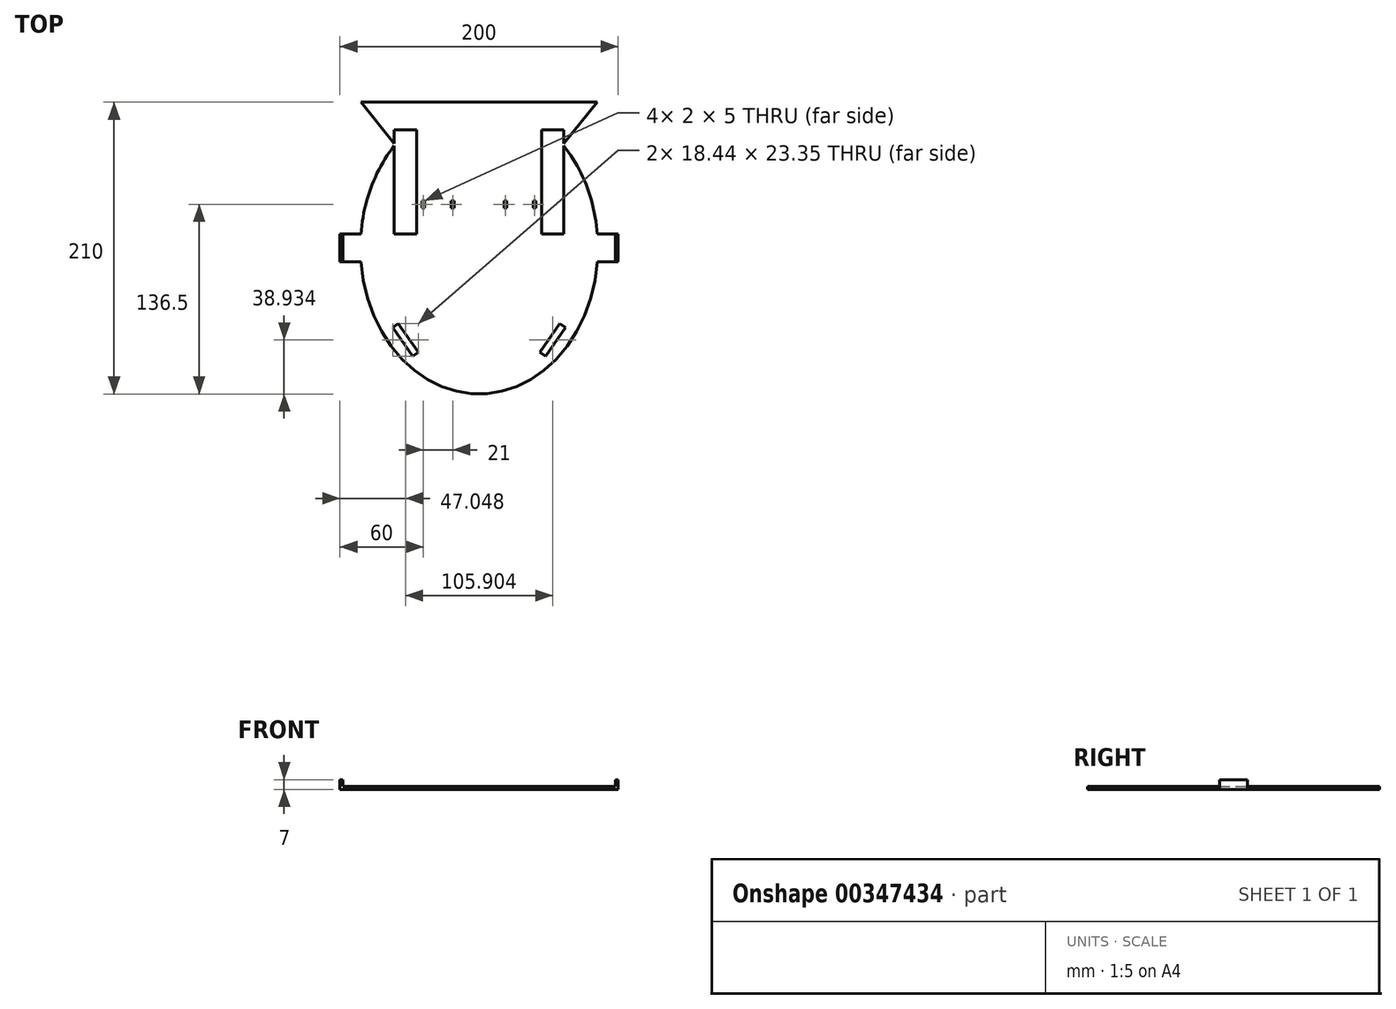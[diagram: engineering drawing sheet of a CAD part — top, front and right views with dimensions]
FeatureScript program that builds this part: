
annotation { "Feature Type Name" : "Feature", "Feature Type Description" : "" }
export const myFeature = defineFeature(function(context is Context, id is Id, definition is map)
    precondition{}
    {
        {
            var Q0;
            Q0=qCreatedBy(makeId("Top.planeOp"),FACE);
            var sketch = newSketch(context, id + "F0", { "sketchPlane" : qUnion([Q0])});
            skLineSegment(sketch, "E0.bottom", {"start": v(0, 0) * mm, "end": v(170, 0) * mm});
            skLineSegment(sketch, "E0.top", {"start": v(0, 210) * mm, "end": v(170, 210) * mm});
            skLineSegment(sketch, "E0.left", {"start": v(0, 0) * mm, "end": v(0, 210) * mm});
            skLineSegment(sketch, "E0.right", {"start": v(170, 0) * mm, "end": v(170, 210) * mm});
            skLineSegment(sketch, "E1", {"start": v(-48.12, 105) * mm, "end": v(198.12, 105) * mm, "construction": true});
            skSolve(sketch);
        }
        {
            var Q0;
            Q0=makeQuery(id+"F0.imprint","IMPRINT",FACE,{"disambiguationData":[TD([[makeQuery(id+"F0.imprint","IMPRINT",EDGE,{"derivedFrom":sQuery(id+"F0.wireOp",EDGE,"E0.bottom")}),1.0]])]});
            extrude(context, id + "F1", {"entities" : qUnion([Q0]), "depth" : 2 * mm});
        }
        {
            var Q0;
            Q0=makeQuery(id+"F1.opExtrude","CAP_FACE",FACE,{"disambiguationData":[OSD([sQuery(id+"F0.wireOp",EDGE,"E0.bottom"),sQuery(id+"F0.wireOp",EDGE,"E0.top"),sQuery(id+"F0.wireOp",EDGE,"E0.left"),sQuery(id+"F0.wireOp",EDGE,"E0.right")])],"isStart":false});
            var sketch = newSketch(context, id + "F2", { "sketchPlane" : qUnion([Q0])});
            skLineSegment(sketch, "E2.bottom", {"start": v(0, 95) * mm, "end": v(-15, 95) * mm});
            skLineSegment(sketch, "E2.top", {"start": v(0, 115) * mm, "end": v(-15, 115) * mm});
            skLineSegment(sketch, "E2.left", {"start": v(0, 95) * mm, "end": v(0, 115) * mm});
            skLineSegment(sketch, "E2.right", {"start": v(-15, 95) * mm, "end": v(-15, 115) * mm});
            skLineSegment(sketch, "E3.bottom", {"start": v(170, 95) * mm, "end": v(185, 95) * mm});
            skLineSegment(sketch, "E3.top", {"start": v(170, 115) * mm, "end": v(185, 115) * mm});
            skLineSegment(sketch, "E3.left", {"start": v(170, 95) * mm, "end": v(170, 115) * mm});
            skLineSegment(sketch, "E3.right", {"start": v(185, 95) * mm, "end": v(185, 115) * mm});
            skSolve(sketch);
        }
        {
            var Q0;
            Q0=makeQuery(id+"F2.imprint","IMPRINT",FACE,{"disambiguationData":[TD([[makeQuery(id+"F2.imprint","IMPRINT",EDGE,{"derivedFrom":sQuery(id+"F2.wireOp",EDGE,"E2.bottom")}),-1.0]])]});
            var Q1;
            Q1=makeQuery(id+"F2.imprint","IMPRINT",FACE,{"disambiguationData":[TD([[makeQuery(id+"F2.imprint","IMPRINT",EDGE,{"derivedFrom":sQuery(id+"F2.wireOp",EDGE,"E3.bottom")}),1.0]])]});
            extrude(context, id + "F3", {"entities" : qUnion([Q0, Q1]), "operationType" : NewBodyOperationType.ADD, "oppositeDirection" : true, "depth" : 2 * mm});
        }
        {
            var Q0;
            Q0=makeQuery(id+"F3.boolean.opBoolean","MERGE",FACE,{"derivedFrom":[makeQuery(id+"F1.opExtrude","CAP_FACE",FACE,{"disambiguationData":[OSD([sQuery(id+"F0.wireOp",EDGE,"E0.bottom"),sQuery(id+"F0.wireOp",EDGE,"E0.top"),sQuery(id+"F0.wireOp",EDGE,"E0.left"),sQuery(id+"F0.wireOp",EDGE,"E0.right")])],"isStart":false}),makeQuery(id+"F3.opExtrude","CAP_FACE",FACE,{"disambiguationData":[OSD([sQuery(id+"F2.wireOp",EDGE,"E2.bottom"),sQuery(id+"F2.wireOp",EDGE,"E2.top"),sQuery(id+"F2.wireOp",EDGE,"E2.left"),sQuery(id+"F2.wireOp",EDGE,"E2.right")])],"isStart":true}),makeQuery(id+"F3.opExtrude","CAP_FACE",FACE,{"disambiguationData":[OSD([sQuery(id+"F2.wireOp",EDGE,"E3.bottom"),sQuery(id+"F2.wireOp",EDGE,"E3.top"),sQuery(id+"F2.wireOp",EDGE,"E3.left"),sQuery(id+"F2.wireOp",EDGE,"E3.right")])],"isStart":true})]});
            var sketch = newSketch(context, id + "F4", { "sketchPlane" : qUnion([Q0])});
            skLineSegment(sketch, "E4.bottom", {"start": v(-15, 95) * mm, "end": v(-13, 95) * mm});
            skLineSegment(sketch, "E4.top", {"start": v(-15, 115) * mm, "end": v(-13, 115) * mm});
            skLineSegment(sketch, "E4.left", {"start": v(-15, 95) * mm, "end": v(-15, 115) * mm});
            skLineSegment(sketch, "E4.right", {"start": v(-13, 95) * mm, "end": v(-13, 115) * mm});
            skLineSegment(sketch, "E5.bottom", {"start": v(185, 95) * mm, "end": v(183, 95) * mm});
            skLineSegment(sketch, "E5.top", {"start": v(185, 115) * mm, "end": v(183, 115) * mm});
            skLineSegment(sketch, "E5.left", {"start": v(185, 95) * mm, "end": v(185, 115) * mm});
            skLineSegment(sketch, "E5.right", {"start": v(183, 95) * mm, "end": v(183, 115) * mm});
            skSolve(sketch);
        }
        {
            var Q0;
            Q0=makeQuery(id+"F4.imprint","IMPRINT",FACE,{"disambiguationData":[TD([[makeQuery(id+"F4.imprint","IMPRINT",EDGE,{"derivedFrom":sQuery(id+"F4.wireOp",EDGE,"E5.bottom")}),1.0]])]});
            var Q1;
            Q1=makeQuery(id+"F4.imprint","IMPRINT",FACE,{"disambiguationData":[TD([[makeQuery(id+"F4.imprint","IMPRINT",EDGE,{"derivedFrom":sQuery(id+"F4.wireOp",EDGE,"E4.bottom")}),-1.0]])]});
            extrude(context, id + "F5", {"entities" : qUnion([Q0, Q1]), "operationType" : NewBodyOperationType.ADD, "depth" : 5 * mm});
        }
        {
            var Q0;
            Q0=makeQuery(id+"F3.boolean.opBoolean","MERGE",FACE,{"derivedFrom":[makeQuery(id+"F1.opExtrude","CAP_FACE",FACE,{"disambiguationData":[OSD([sQuery(id+"F0.wireOp",EDGE,"E0.bottom"),sQuery(id+"F0.wireOp",EDGE,"E0.top"),sQuery(id+"F0.wireOp",EDGE,"E0.left"),sQuery(id+"F0.wireOp",EDGE,"E0.right")])],"isStart":false}),makeQuery(id+"F3.opExtrude","CAP_FACE",FACE,{"disambiguationData":[OSD([sQuery(id+"F2.wireOp",EDGE,"E2.bottom"),sQuery(id+"F2.wireOp",EDGE,"E2.top"),sQuery(id+"F2.wireOp",EDGE,"E2.left"),sQuery(id+"F2.wireOp",EDGE,"E2.right")])],"isStart":true}),makeQuery(id+"F3.opExtrude","CAP_FACE",FACE,{"disambiguationData":[OSD([sQuery(id+"F2.wireOp",EDGE,"E3.bottom"),sQuery(id+"F2.wireOp",EDGE,"E3.top"),sQuery(id+"F2.wireOp",EDGE,"E3.left"),sQuery(id+"F2.wireOp",EDGE,"E3.right")])],"isStart":true})]});
            var sketch = newSketch(context, id + "F6", { "sketchPlane" : qUnion([Q0])});
            skEllipse(sketch, "E6", {"center": v(85, 105) * mm, "majorRadius": 105 * mm, "minorRadius": 85.39 * mm, "majorAxis": v(0, -1)});
            skLineSegment(sketch, "E7", {"start": v(0, 210) * mm, "end": v(170, 0) * mm});
            skLineSegment(sketch, "E8", {"start": v(170, 0) * mm, "end": v(0, 0) * mm});
            skLineSegment(sketch, "E9", {"start": v(0, 0) * mm, "end": v(170, 210) * mm});
            skSolve(sketch);
        }
        {
            var Q0;
            {var subQ2=sQuery(id+"F0.wireOp",EDGE,"E0.left");var subQ3=sQuery(id+"F0.wireOp",EDGE,"E0.top");var subQ4=makeQuery(id+"F3.boolean.opBoolean","SPLIT",EDGE,{"disambiguationData":[TD([makeQuery(id+"F1.opExtrude","SWEPT_FACE",FACE,{"disambiguationData":[OSD([subQ3])]})])],"derivedFrom":makeQuery(id+"F1.opExtrude","CAP_EDGE",EDGE,{"disambiguationData":[OSD([subQ2])],"isStart":false})});Q0=makeQuery(id+"F6.imprint","IMPRINT",FACE,{"disambiguationData":[TD([[makeQuery(id+"F6.imprint","IMPRINT",EDGE,{"derivedFrom":subQ4}),-1.0]])]});}
            var Q1;
            {var subQ0=sQuery(id+"F6.wireOp",EDGE,"E7");var subQ1=sQuery(id+"F6.wireOp",EDGE,"E6");var subQ2=makeQuery(id+"F6.imprint","INTERSECT",VERTEX,{"disambiguationData":[OD(1.0)],"derivedFrom":[subQ1,subQ0]});Q1=makeQuery(id+"F6.imprint","IMPRINT",FACE,{"disambiguationData":[TD([[makeQuery(id+"F6.imprint","IMPRINT",EDGE,{"disambiguationData":[TD([[subQ2,1.0]])],"derivedFrom":subQ1}),-1.0]])]});}
            var Q2;
            {var subQ0=sQuery(id+"F6.wireOp",EDGE,"E9");var subQ1=sQuery(id+"F6.wireOp",EDGE,"E6");var subQ2=makeQuery(id+"F6.imprint","INTERSECT",VERTEX,{"disambiguationData":[OD(0.0)],"derivedFrom":[subQ1,subQ0]});Q2=makeQuery(id+"F6.imprint","IMPRINT",FACE,{"disambiguationData":[TD([[makeQuery(id+"F6.imprint","IMPRINT",EDGE,{"disambiguationData":[TD([[subQ2,-1.0]])],"derivedFrom":subQ1}),-1.0]])]});}
            var Q3;
            {var subQ2=sQuery(id+"F0.wireOp",EDGE,"E0.right");var subQ3=sQuery(id+"F0.wireOp",EDGE,"E0.top");var subQ4=makeQuery(id+"F3.boolean.opBoolean","SPLIT",EDGE,{"disambiguationData":[TD([makeQuery(id+"F1.opExtrude","SWEPT_FACE",FACE,{"disambiguationData":[OSD([subQ3])]})])],"derivedFrom":makeQuery(id+"F1.opExtrude","CAP_EDGE",EDGE,{"disambiguationData":[OSD([subQ2])],"isStart":false})});Q3=makeQuery(id+"F6.imprint","IMPRINT",FACE,{"disambiguationData":[TD([[makeQuery(id+"F6.imprint","IMPRINT",EDGE,{"derivedFrom":subQ4}),1.0]])]});}
            var Q4;
            {var subQ2=sQuery(id+"F0.wireOp",EDGE,"E0.left");var subQ3=sQuery(id+"F0.wireOp",EDGE,"E0.bottom");var subQ4=makeQuery(id+"F3.boolean.opBoolean","SPLIT",EDGE,{"disambiguationData":[TD([makeQuery(id+"F1.opExtrude","SWEPT_FACE",FACE,{"disambiguationData":[OSD([subQ3])]})])],"derivedFrom":makeQuery(id+"F1.opExtrude","CAP_EDGE",EDGE,{"disambiguationData":[OSD([subQ2])],"isStart":false})});Q4=makeQuery(id+"F6.imprint","IMPRINT",FACE,{"disambiguationData":[TD([[makeQuery(id+"F6.imprint","IMPRINT",EDGE,{"derivedFrom":subQ4}),-1.0]])]});}
            var Q5;
            {var subQ0=sQuery(id+"F6.wireOp",EDGE,"E8");var subQ1=sQuery(id+"F6.wireOp",EDGE,"E6");var subQ2=makeQuery(id+"F6.imprint","INTERSECT",VERTEX,{"derivedFrom":[subQ1,subQ0]});Q5=makeQuery(id+"F6.imprint","IMPRINT",FACE,{"disambiguationData":[TD([[makeQuery(id+"F6.imprint","IMPRINT",EDGE,{"disambiguationData":[TD([[subQ2,1.0]])],"derivedFrom":subQ1}),-1.0]])]});}
            var Q6;
            {var subQ0=sQuery(id+"F6.wireOp",EDGE,"E8");var subQ1=sQuery(id+"F6.wireOp",EDGE,"E6");var subQ2=makeQuery(id+"F6.imprint","INTERSECT",VERTEX,{"derivedFrom":[subQ1,subQ0]});Q6=makeQuery(id+"F6.imprint","IMPRINT",FACE,{"disambiguationData":[TD([[makeQuery(id+"F6.imprint","IMPRINT",EDGE,{"disambiguationData":[TD([[subQ2,-1.0]])],"derivedFrom":subQ1}),-1.0]])]});}
            var Q7;
            {var subQ2=sQuery(id+"F0.wireOp",EDGE,"E0.right");var subQ3=sQuery(id+"F0.wireOp",EDGE,"E0.bottom");var subQ4=makeQuery(id+"F3.boolean.opBoolean","SPLIT",EDGE,{"disambiguationData":[TD([makeQuery(id+"F1.opExtrude","SWEPT_FACE",FACE,{"disambiguationData":[OSD([subQ3])]})])],"derivedFrom":makeQuery(id+"F1.opExtrude","CAP_EDGE",EDGE,{"disambiguationData":[OSD([subQ2])],"isStart":false})});Q7=makeQuery(id+"F6.imprint","IMPRINT",FACE,{"disambiguationData":[TD([[makeQuery(id+"F6.imprint","IMPRINT",EDGE,{"derivedFrom":subQ4}),1.0]])]});}
            extrude(context, id + "F7", {"entities" : qUnion([Q0, Q1, Q2, Q3, Q4, Q5, Q6, Q7]), "operationType" : NewBodyOperationType.REMOVE, "endBound" : BoundingType.THROUGH_ALL, "oppositeDirection" : true, "depth" : 25 * mm});
        }
        {
            var Q0;
            Q0=makeQuery(id+"F3.boolean.opBoolean","MERGE",FACE,{"derivedFrom":[makeQuery(id+"F1.opExtrude","CAP_FACE",FACE,{"disambiguationData":[OSD([sQuery(id+"F0.wireOp",EDGE,"E0.bottom"),sQuery(id+"F0.wireOp",EDGE,"E0.top"),sQuery(id+"F0.wireOp",EDGE,"E0.left"),sQuery(id+"F0.wireOp",EDGE,"E0.right")])],"isStart":false}),makeQuery(id+"F3.opExtrude","CAP_FACE",FACE,{"disambiguationData":[OSD([sQuery(id+"F2.wireOp",EDGE,"E2.bottom"),sQuery(id+"F2.wireOp",EDGE,"E2.top"),sQuery(id+"F2.wireOp",EDGE,"E2.left"),sQuery(id+"F2.wireOp",EDGE,"E2.right")])],"isStart":true}),makeQuery(id+"F3.opExtrude","CAP_FACE",FACE,{"disambiguationData":[OSD([sQuery(id+"F2.wireOp",EDGE,"E3.bottom"),sQuery(id+"F2.wireOp",EDGE,"E3.top"),sQuery(id+"F2.wireOp",EDGE,"E3.left"),sQuery(id+"F2.wireOp",EDGE,"E3.right")])],"isStart":true})]});
            var sketch = newSketch(context, id + "F8", { "sketchPlane" : qUnion([Q0])});
            skLineSegment(sketch, "E10.bottom", {"start": v(30, 172.5) * mm, "end": v(140, 172.5) * mm});
            skLineSegment(sketch, "E10.top", {"start": v(30, 37.5) * mm, "end": v(140, 37.5) * mm});
            skLineSegment(sketch, "E10.left", {"start": v(30, 172.5) * mm, "end": v(30, 37.5) * mm});
            skLineSegment(sketch, "E10.right", {"start": v(140, 172.5) * mm, "end": v(140, 37.5) * mm});
            skLineSegment(sketch, "E11", {"start": v(85, 210) * mm, "end": v(85, 0) * mm});
            skLineSegment(sketch, "E12", {"start": v(-13, 105) * mm, "end": v(183, 105) * mm});
            skLineSegment(sketch, "E13.MirrorCS", {"start": v(140, 172.5) * mm, "end": v(30, 172.5) * mm});
            skLineSegment(sketch, "E14.MirrorCS", {"start": v(140, 37.5) * mm, "end": v(140, 172.5) * mm});
            skLineSegment(sketch, "E15.MirrorCS", {"start": v(140, 37.5) * mm, "end": v(30, 37.5) * mm});
            skLineSegment(sketch, "E16", {"start": v(147.17, 47.74) * mm, "end": v(132.83, 27.26) * mm});
            skLineSegment(sketch, "E17", {"start": v(132.83, 27.26) * mm, "end": v(128.73, 30.13) * mm});
            skLineSegment(sketch, "E18", {"start": v(128.73, 30.13) * mm, "end": v(143.07, 50.6) * mm});
            skLineSegment(sketch, "E19", {"start": v(143.07, 50.6) * mm, "end": v(147.17, 47.74) * mm});
            skLineSegment(sketch, "E20", {"start": v(140, 37.5) * mm, "end": v(135.9, 40.37) * mm});
            skLineSegment(sketch, "E21.MirrorCS", {"start": v(26.93, 50.6) * mm, "end": v(22.83, 47.74) * mm});
            skLineSegment(sketch, "E22.MirrorCS", {"start": v(41.27, 30.13) * mm, "end": v(26.93, 50.6) * mm});
            skLineSegment(sketch, "E23.MirrorCS", {"start": v(22.83, 47.74) * mm, "end": v(37.17, 27.26) * mm});
            skLineSegment(sketch, "E24.MirrorCS", {"start": v(30, 37.5) * mm, "end": v(34.1, 40.37) * mm});
            skLineSegment(sketch, "E25.MirrorCS", {"start": v(37.17, 27.26) * mm, "end": v(41.27, 30.13) * mm});
            skSolve(sketch);
        }
        {
            var Q0;
            {var subQ5=sQuery(id+"F8.wireOp",EDGE,"E17");Q0=makeQuery(id+"F8.imprint","IMPRINT",FACE,{"disambiguationData":[TD([[makeQuery(id+"F8.imprint","IMPRINT",EDGE,{"derivedFrom":subQ5}),-1.0]])]});}
            var Q1;
            {var subQ0=sQuery(id+"F8.wireOp",EDGE,"E20");Q1=makeQuery(id+"F8.imprint","IMPRINT",FACE,{"disambiguationData":[TD([[makeQuery(id+"F8.imprint","IMPRINT",EDGE,{"derivedFrom":subQ0}),1.0]])]});}
            var Q2;
            {var subQ0=sQuery(id+"F8.wireOp",EDGE,"E20");Q2=makeQuery(id+"F8.imprint","IMPRINT",FACE,{"disambiguationData":[TD([[makeQuery(id+"F8.imprint","IMPRINT",EDGE,{"derivedFrom":subQ0}),-1.0]])]});}
            var Q3;
            {var subQ5=sQuery(id+"F8.wireOp",EDGE,"E19");Q3=makeQuery(id+"F8.imprint","IMPRINT",FACE,{"disambiguationData":[TD([[makeQuery(id+"F8.imprint","IMPRINT",EDGE,{"derivedFrom":subQ5}),-1.0]])]});}
            var Q4;
            {var subQ5=sQuery(id+"F8.wireOp",EDGE,"E25.MirrorCS");Q4=makeQuery(id+"F8.imprint","IMPRINT",FACE,{"disambiguationData":[TD([[makeQuery(id+"F8.imprint","IMPRINT",EDGE,{"derivedFrom":subQ5}),1.0]])]});}
            var Q5;
            {var subQ0=sQuery(id+"F8.wireOp",EDGE,"E24.MirrorCS");Q5=makeQuery(id+"F8.imprint","IMPRINT",FACE,{"disambiguationData":[TD([[makeQuery(id+"F8.imprint","IMPRINT",EDGE,{"derivedFrom":subQ0}),-1.0]])]});}
            var Q6;
            {var subQ0=sQuery(id+"F8.wireOp",EDGE,"E24.MirrorCS");Q6=makeQuery(id+"F8.imprint","IMPRINT",FACE,{"disambiguationData":[TD([[makeQuery(id+"F8.imprint","IMPRINT",EDGE,{"derivedFrom":subQ0}),1.0]])]});}
            var Q7;
            {var subQ5=sQuery(id+"F8.wireOp",EDGE,"E21.MirrorCS");Q7=makeQuery(id+"F8.imprint","IMPRINT",FACE,{"disambiguationData":[TD([[makeQuery(id+"F8.imprint","IMPRINT",EDGE,{"derivedFrom":subQ5}),1.0]])]});}
            extrude(context, id + "F9", {"entities" : qUnion([Q0, Q1, Q2, Q3, Q4, Q5, Q6, Q7]), "operationType" : NewBodyOperationType.REMOVE, "endBound" : BoundingType.THROUGH_ALL, "oppositeDirection" : true, "depth" : 25 * mm});
        }
        {
            var Q0;
            Q0=makeQuery(id+"F3.boolean.opBoolean","MERGE",FACE,{"derivedFrom":[makeQuery(id+"F1.opExtrude","CAP_FACE",FACE,{"disambiguationData":[OSD([sQuery(id+"F0.wireOp",EDGE,"E0.bottom"),sQuery(id+"F0.wireOp",EDGE,"E0.top"),sQuery(id+"F0.wireOp",EDGE,"E0.left"),sQuery(id+"F0.wireOp",EDGE,"E0.right")])],"isStart":false}),makeQuery(id+"F3.opExtrude","CAP_FACE",FACE,{"disambiguationData":[OSD([sQuery(id+"F2.wireOp",EDGE,"E2.bottom"),sQuery(id+"F2.wireOp",EDGE,"E2.top"),sQuery(id+"F2.wireOp",EDGE,"E2.left"),sQuery(id+"F2.wireOp",EDGE,"E2.right")])],"isStart":true}),makeQuery(id+"F3.opExtrude","CAP_FACE",FACE,{"disambiguationData":[OSD([sQuery(id+"F2.wireOp",EDGE,"E3.bottom"),sQuery(id+"F2.wireOp",EDGE,"E3.top"),sQuery(id+"F2.wireOp",EDGE,"E3.left"),sQuery(id+"F2.wireOp",EDGE,"E3.right")])],"isStart":true})]});
            var sketch = newSketch(context, id + "F10", { "sketchPlane" : qUnion([Q0])});
            skLineSegment(sketch, "E26.bottom", {"start": v(24, 190) * mm, "end": v(40, 190) * mm});
            skLineSegment(sketch, "E26.top", {"start": v(24, 115) * mm, "end": v(40, 115) * mm});
            skLineSegment(sketch, "E26.left", {"start": v(24, 190) * mm, "end": v(24, 115) * mm});
            skLineSegment(sketch, "E26.right", {"start": v(40, 190) * mm, "end": v(40, 115) * mm});
            skLineSegment(sketch, "E27", {"start": v(85, 210) * mm, "end": v(85, 0) * mm});
            skLineSegment(sketch, "E28.MirrorCS", {"start": v(146, 190) * mm, "end": v(146, 115) * mm});
            skLineSegment(sketch, "E29.MirrorCS", {"start": v(146, 115) * mm, "end": v(130, 115) * mm});
            skLineSegment(sketch, "E30.MirrorCS", {"start": v(146, 190) * mm, "end": v(130, 190) * mm});
            skLineSegment(sketch, "E31.MirrorCS", {"start": v(130, 190) * mm, "end": v(130, 115) * mm});
            skLineSegment(sketch, "E32", {"start": v(40, 190) * mm, "end": v(40, 194.24) * mm});
            skLineSegment(sketch, "E33", {"start": v(130, 190) * mm, "end": v(130, 194.24) * mm});
            skSolve(sketch);
        }
        {
            var Q0;
            {var subQ19=sQuery(id+"F10.wireOp",EDGE,"E29.MirrorCS");Q0=makeQuery(id+"F10.imprint","IMPRINT",FACE,{"disambiguationData":[TD([[makeQuery(id+"F10.imprint","IMPRINT",EDGE,{"derivedFrom":subQ19}),-1.0]])]});}
            var Q1;
            {var subQ2=sQuery(id+"F10.wireOp",EDGE,"E26.top");Q1=makeQuery(id+"F10.imprint","IMPRINT",FACE,{"disambiguationData":[TD([[makeQuery(id+"F10.imprint","IMPRINT",EDGE,{"derivedFrom":subQ2}),1.0]])]});}
            var Q2;
            {var subQ0=sQuery(id+"F10.wireOp",EDGE,"E32");Q2=makeQuery(id+"F10.imprint","IMPRINT",FACE,{"disambiguationData":[TD([[makeQuery(id+"F10.imprint","IMPRINT",EDGE,{"derivedFrom":subQ0}),1.0]])]});}
            var Q3;
            {var subQ0=sQuery(id+"F10.wireOp",EDGE,"E33");Q3=makeQuery(id+"F10.imprint","IMPRINT",FACE,{"disambiguationData":[TD([[makeQuery(id+"F10.imprint","IMPRINT",EDGE,{"derivedFrom":subQ0}),-1.0]])]});}
            extrude(context, id + "F11", {"entities" : qUnion([Q0, Q1, Q2, Q3]), "operationType" : NewBodyOperationType.REMOVE, "endBound" : BoundingType.THROUGH_ALL, "oppositeDirection" : true, "depth" : 25 * mm});
        }
        {
            var Q0;
            Q0=makeQuery(id+"F3.boolean.opBoolean","MERGE",FACE,{"derivedFrom":[makeQuery(id+"F1.opExtrude","CAP_FACE",FACE,{"disambiguationData":[OSD([sQuery(id+"F0.wireOp",EDGE,"E0.bottom"),sQuery(id+"F0.wireOp",EDGE,"E0.top"),sQuery(id+"F0.wireOp",EDGE,"E0.left"),sQuery(id+"F0.wireOp",EDGE,"E0.right")])],"isStart":false}),makeQuery(id+"F3.opExtrude","CAP_FACE",FACE,{"disambiguationData":[OSD([sQuery(id+"F2.wireOp",EDGE,"E2.bottom"),sQuery(id+"F2.wireOp",EDGE,"E2.top"),sQuery(id+"F2.wireOp",EDGE,"E2.left"),sQuery(id+"F2.wireOp",EDGE,"E2.right")])],"isStart":true}),makeQuery(id+"F3.opExtrude","CAP_FACE",FACE,{"disambiguationData":[OSD([sQuery(id+"F2.wireOp",EDGE,"E3.bottom"),sQuery(id+"F2.wireOp",EDGE,"E3.top"),sQuery(id+"F2.wireOp",EDGE,"E3.left"),sQuery(id+"F2.wireOp",EDGE,"E3.right")])],"isStart":true})]});
            var sketch = newSketch(context, id + "F12", { "sketchPlane" : qUnion([Q0])});
            skLineSegment(sketch, "E34.bottom", {"start": v(44, 139) * mm, "end": v(46, 139) * mm});
            skLineSegment(sketch, "E34.top", {"start": v(44, 134) * mm, "end": v(46, 134) * mm});
            skLineSegment(sketch, "E34.left", {"start": v(44, 139) * mm, "end": v(44, 134) * mm});
            skLineSegment(sketch, "E34.right", {"start": v(46, 139) * mm, "end": v(46, 134) * mm});
            skLineSegment(sketch, "E35.bottom", {"start": v(65, 134) * mm, "end": v(67, 134) * mm});
            skLineSegment(sketch, "E35.top", {"start": v(65, 139) * mm, "end": v(67, 139) * mm});
            skLineSegment(sketch, "E35.left", {"start": v(65, 134) * mm, "end": v(65, 139) * mm});
            skLineSegment(sketch, "E35.right", {"start": v(67, 134) * mm, "end": v(67, 139) * mm});
            skLineSegment(sketch, "E36", {"start": v(85, 210) * mm, "end": v(85, 0) * mm});
            skLineSegment(sketch, "E37.MirrorCS", {"start": v(105, 139) * mm, "end": v(103, 139) * mm});
            skLineSegment(sketch, "E38.MirrorCS", {"start": v(105, 134) * mm, "end": v(103, 134) * mm});
            skLineSegment(sketch, "E39.MirrorCS", {"start": v(126, 139) * mm, "end": v(124, 139) * mm});
            skLineSegment(sketch, "E40.MirrorCS", {"start": v(126, 134) * mm, "end": v(124, 134) * mm});
            skLineSegment(sketch, "E41.MirrorCS", {"start": v(103, 134) * mm, "end": v(103, 139) * mm});
            skLineSegment(sketch, "E42.MirrorCS", {"start": v(105, 134) * mm, "end": v(105, 139) * mm});
            skLineSegment(sketch, "E43.MirrorCS", {"start": v(124, 139) * mm, "end": v(124, 134) * mm});
            skLineSegment(sketch, "E44.MirrorCS", {"start": v(126, 139) * mm, "end": v(126, 134) * mm});
            skSolve(sketch);
        }
        {
            var Q0;
            Q0=makeQuery(id+"F12.imprint","IMPRINT",FACE,{"disambiguationData":[TD([[makeQuery(id+"F12.imprint","IMPRINT",EDGE,{"derivedFrom":sQuery(id+"F12.wireOp",EDGE,"E34.bottom")}),-1.0]])]});
            var Q1;
            Q1=makeQuery(id+"F12.imprint","IMPRINT",FACE,{"disambiguationData":[TD([[makeQuery(id+"F12.imprint","IMPRINT",EDGE,{"derivedFrom":sQuery(id+"F12.wireOp",EDGE,"E35.bottom")}),1.0]])]});
            var Q2;
            Q2=makeQuery(id+"F12.imprint","IMPRINT",FACE,{"disambiguationData":[TD([[makeQuery(id+"F12.imprint","IMPRINT",EDGE,{"derivedFrom":sQuery(id+"F12.wireOp",EDGE,"E37.MirrorCS")}),1.0]])]});
            var Q3;
            Q3=makeQuery(id+"F12.imprint","IMPRINT",FACE,{"disambiguationData":[TD([[makeQuery(id+"F12.imprint","IMPRINT",EDGE,{"derivedFrom":sQuery(id+"F12.wireOp",EDGE,"E39.MirrorCS")}),1.0]])]});
            extrude(context, id + "F13", {"entities" : qUnion([Q0, Q1, Q2, Q3]), "operationType" : NewBodyOperationType.REMOVE, "endBound" : BoundingType.THROUGH_ALL, "oppositeDirection" : true, "depth" : 25 * mm});
        }
    });
